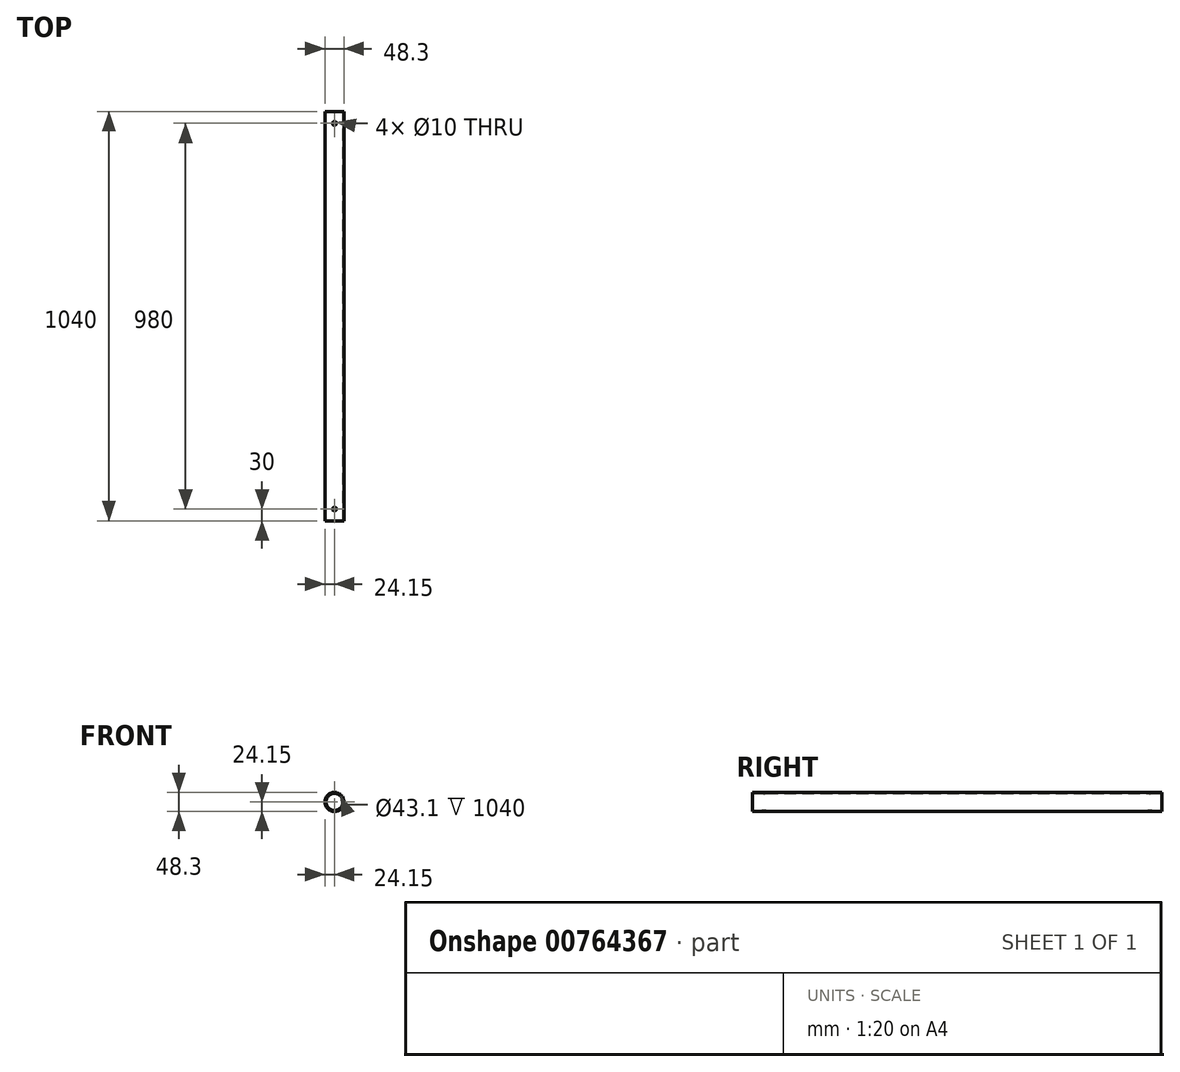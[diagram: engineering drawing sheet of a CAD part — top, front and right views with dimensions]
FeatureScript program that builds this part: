
annotation { "Feature Type Name" : "Feature", "Feature Type Description" : "" }
export const myFeature = defineFeature(function(context is Context, id is Id, definition is map)
    precondition{}
    {
        {
            var Q0;
            Q0=qCreatedBy(makeId("Front.planeOp"),FACE);
            var sketch = newSketch(context, id + "F0", { "sketchPlane" : qUnion([Q0])});
            skCircle(sketch, "E0", {"center": v(0, 0) * mm, "radius": 24.15 * mm});
            skCircle(sketch, "E1.0", {"center": v(0, 0) * mm, "radius": 21.55 * mm});
            skSolve(sketch);
        }
        {
            var Q0;
            Q0=makeQuery(id+"F0.imprint","IMPRINT",FACE,{"disambiguationData":[TD([[makeQuery(id+"F0.imprint","IMPRINT",EDGE,{"derivedFrom":sQuery(id+"F0.wireOp",EDGE,"E0")}),1.0]])]});
            extrude(context, id + "F1", {"entities" : qUnion([Q0]), "depth" : 1040 * mm, "offsetDistance" : 25 * mm, "symmetric" : true});
        }
        {
            var Q0;
            Q0=qCreatedBy(makeId("Top.planeOp"),FACE);
            cPlane(context, id + "F2", {"entities" : qUnion([Q0]), "cplaneType" : CPlaneType.OFFSET, "offset" : 24.15 * mm, "width" : 150 * mm, "height" : 150 * mm});
        }
        {
            var Q0;
            Q0=qCreatedBy(id+"F2.planeOp",FACE);
            var sketch = newSketch(context, id + "F3", { "sketchPlane" : qUnion([Q0])});
            skCircle(sketch, "E2", {"center": v(0, 490) * mm, "radius": 5 * mm});
            skCircle(sketch, "E3", {"center": v(0, -490) * mm, "radius": 5 * mm});
            skSolve(sketch);
        }
        {
            var Q0;
            Q0=sQuery(id+"F3.wireOp",VERTEX,"E3.center");
            var Q1;
            Q1=sQuery(id+"F3.wireOp",VERTEX,"E2.center");
            var Q2;
            Q2=makeQuery(id+"F1.opExtrude","SWEPT_BODY",BODY,{"disambiguationData":[OSD([sQuery(id+"F0.wireOp",EDGE,"E0"),sQuery(id+"F0.wireOp",EDGE,"E1.0")])]});
            hole(context, id + "F4", {"style" : HoleStyle.SIMPLE, "endStyle" : HoleEndStyle.THROUGH, "holeDiameter" : 10 * mm, "majorDiameter" : 5 * mm, "isTappedThrough" : true, "tappedDepth" : 12 * mm, "tapClearance" : 3, "locations" : qUnion([Q0, Q1]), "scope" : qUnion([Q2]), "startStyle" : HoleStartStyle.PART});
        }
    });
